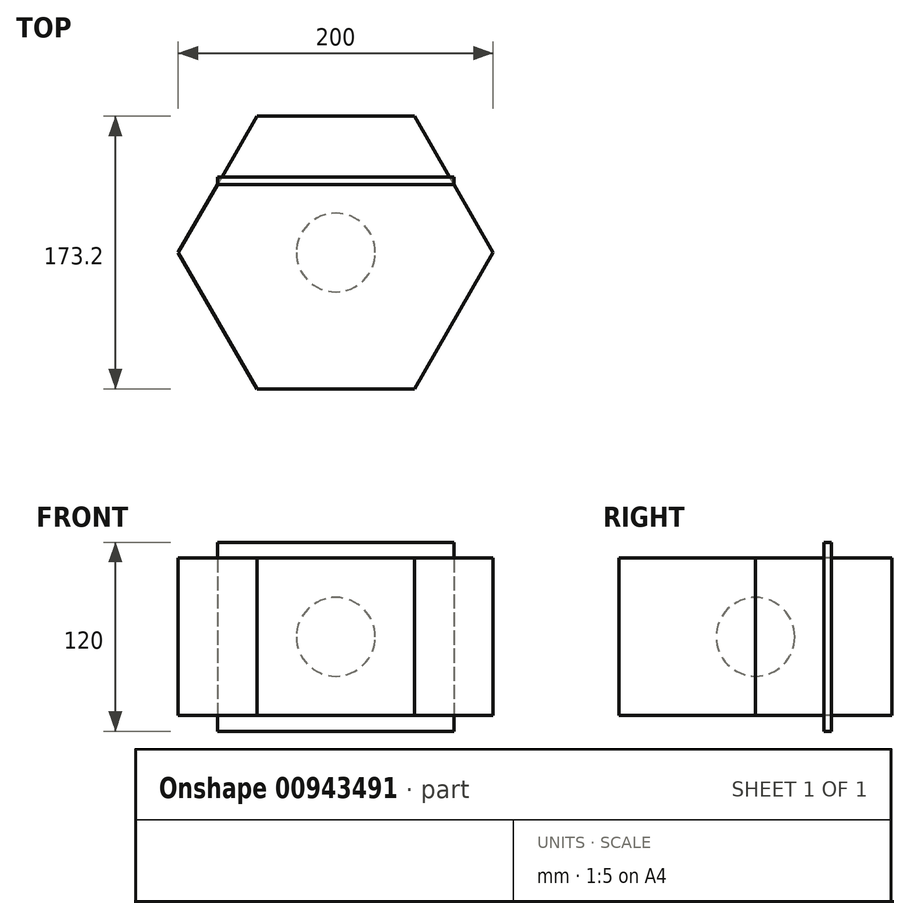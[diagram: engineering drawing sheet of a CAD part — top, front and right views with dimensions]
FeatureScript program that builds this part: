
annotation { "Feature Type Name" : "Feature", "Feature Type Description" : "" }
export const myFeature = defineFeature(function(context is Context, id is Id, definition is map)
    precondition{}
    {
        {
            var Q0;
            Q0=qCreatedBy(makeId("Top.planeOp"),FACE);
            var sketch = newSketch(context, id + "F0", { "sketchPlane" : qUnion([Q0])});
            skCircle(sketch, "E0.cCircle", {"center": v(0, 0) * mm, "radius": 86.6 * mm, "construction": true});
            skLineSegment(sketch, "E0.0", {"start": v(-50, 86.6) * mm, "end": v(50, 86.6) * mm});
            skLineSegment(sketch, "E0.1", {"start": v(50, 86.6) * mm, "end": v(100, 0) * mm});
            skLineSegment(sketch, "E0.2", {"start": v(100, 0) * mm, "end": v(50, -86.6) * mm});
            skLineSegment(sketch, "E0.3", {"start": v(50, -86.6) * mm, "end": v(-50, -86.6) * mm});
            skLineSegment(sketch, "E0.4", {"start": v(-50, -86.6) * mm, "end": v(-100, 0) * mm});
            skLineSegment(sketch, "E0.5", {"start": v(-100, 0) * mm, "end": v(-50, 86.6) * mm});
            skPoint(sketch, "E0.0.midPoint", {"position": v(0, 86.6) * mm});
            skSolve(sketch);
        }
        {
            var Q0;
            Q0=qCreatedBy(makeId("Top.planeOp"),FACE);
            var sketch = newSketch(context, id + "F1", { "sketchPlane" : qUnion([Q0])});
            skLineSegment(sketch, "E1.bottom", {"start": v(-75, 43.3) * mm, "end": v(75, 43.3) * mm});
            skLineSegment(sketch, "E1.top", {"start": v(-75, 48.05) * mm, "end": v(75, 48.05) * mm});
            skLineSegment(sketch, "E1.left", {"start": v(-75, 43.3) * mm, "end": v(-75, 48.05) * mm});
            skLineSegment(sketch, "E1.right", {"start": v(75, 43.3) * mm, "end": v(75, 48.05) * mm});
            skSolve(sketch);
        }
        {
            var Q0;
            Q0=makeQuery(id+"F0.imprint","IMPRINT",FACE,{"disambiguationData":[TD([[makeQuery(id+"F0.imprint","IMPRINT",EDGE,{"derivedFrom":sQuery(id+"F0.wireOp",EDGE,"E0.0")}),-1.0]])]});
            extrude(context, id + "F2", {"entities" : qUnion([Q0]), "endBound" : BoundingType.SYMMETRIC, "depth" : 100 * mm, "offsetDistance" : 25 * mm});
        }
        {
            var Q0;
            Q0=makeQuery(id+"F1.imprint","IMPRINT",FACE,{"disambiguationData":[TD([[makeQuery(id+"F1.imprint","IMPRINT",EDGE,{"derivedFrom":sQuery(id+"F1.wireOp",EDGE,"E1.bottom")}),1.0]])]});
            extrude(context, id + "F3", {"entities" : qUnion([Q0]), "endBound" : BoundingType.SYMMETRIC, "depth" : 120 * mm, "offsetDistance" : 25 * mm});
        }
        {
            var Q0;
            Q0=qCreatedBy(makeId("Front.planeOp"),FACE);
            var sketch = newSketch(context, id + "F4", { "sketchPlane" : qUnion([Q0])});
            skArc(sketch, "E2", {"start": v(-25, 0) * mm, "mid": v(0, -25) * mm, "end": v(25, 0) * mm});
            skLineSegment(sketch, "E3", {"start": v(-25, 0) * mm, "end": v(25, 0) * mm});
            skSolve(sketch);
        }
        {
            var Q0;
            Q0=makeQuery(id+"F4.imprint","IMPRINT",FACE,{"disambiguationData":[TD([[makeQuery(id+"F4.imprint","IMPRINT",EDGE,{"derivedFrom":sQuery(id+"F4.wireOp",EDGE,"E2")}),1.0]])]});
            var Q1;
            Q1=sQuery(id+"F4.wireOp",EDGE,"E3");
            revolve(context, id + "F5", {"surfaceOperationType" : NewSurfaceOperationType.NEW, "entities" : qUnion([Q0]), "axis" : qUnion([Q1]), "revolveType" : RevolveType.FULL});
        }
    });
